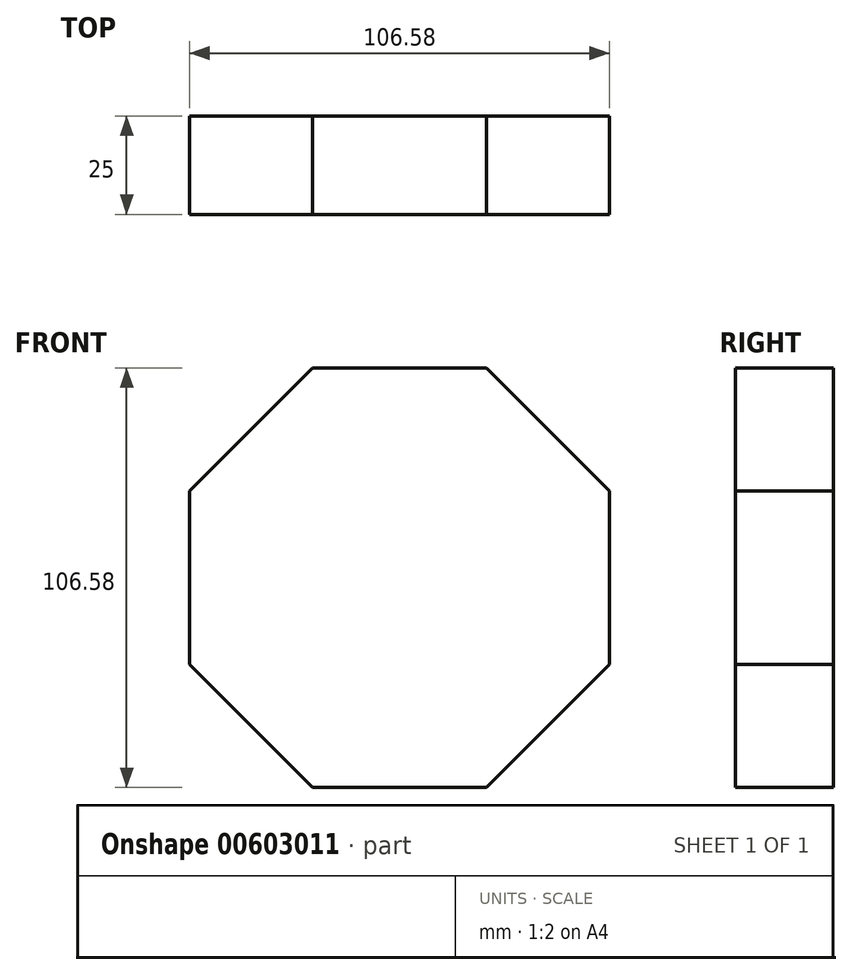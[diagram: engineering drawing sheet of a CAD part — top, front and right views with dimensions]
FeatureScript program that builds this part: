
annotation { "Feature Type Name" : "Feature", "Feature Type Description" : "" }
export const myFeature = defineFeature(function(context is Context, id is Id, definition is map)
    precondition{}
    {
        {
            var Q0;
            Q0=qCreatedBy(makeId("Front.planeOp"),FACE);
            var sketch = newSketch(context, id + "F0", { "sketchPlane" : qUnion([Q0])});
            skCircle(sketch, "E0.cCircle", {"center": v(0, 0) * mm, "radius": 53.29 * mm, "construction": true});
            skLineSegment(sketch, "E0.0", {"start": v(-22.07, 53.29) * mm, "end": v(22.07, 53.29) * mm});
            skLineSegment(sketch, "E0.1", {"start": v(22.07, 53.29) * mm, "end": v(53.29, 22.07) * mm});
            skLineSegment(sketch, "E0.2", {"start": v(53.29, 22.07) * mm, "end": v(53.29, -22.07) * mm});
            skLineSegment(sketch, "E0.3", {"start": v(53.29, -22.07) * mm, "end": v(22.07, -53.29) * mm});
            skLineSegment(sketch, "E0.4", {"start": v(22.07, -53.29) * mm, "end": v(-22.07, -53.29) * mm});
            skLineSegment(sketch, "E0.5", {"start": v(-22.07, -53.29) * mm, "end": v(-53.29, -22.07) * mm});
            skLineSegment(sketch, "E0.6", {"start": v(-53.29, -22.07) * mm, "end": v(-53.29, 22.07) * mm});
            skLineSegment(sketch, "E0.7", {"start": v(-53.29, 22.07) * mm, "end": v(-22.07, 53.29) * mm});
            skPoint(sketch, "E0.0.midPoint", {"position": v(0, 53.29) * mm});
            skSolve(sketch);
        }
        {
            var Q0;
            Q0=makeQuery(id+"F0.imprint","IMPRINT",FACE,{"disambiguationData":[TD([[makeQuery(id+"F0.imprint","IMPRINT",EDGE,{"derivedFrom":sQuery(id+"F0.wireOp",EDGE,"E0.0")}),-1.0]])]});
            extrude(context, id + "F1", {"entities" : qUnion([Q0]), "depth" : 25 * mm, "offsetDistance" : 25 * mm});
        }
    });
